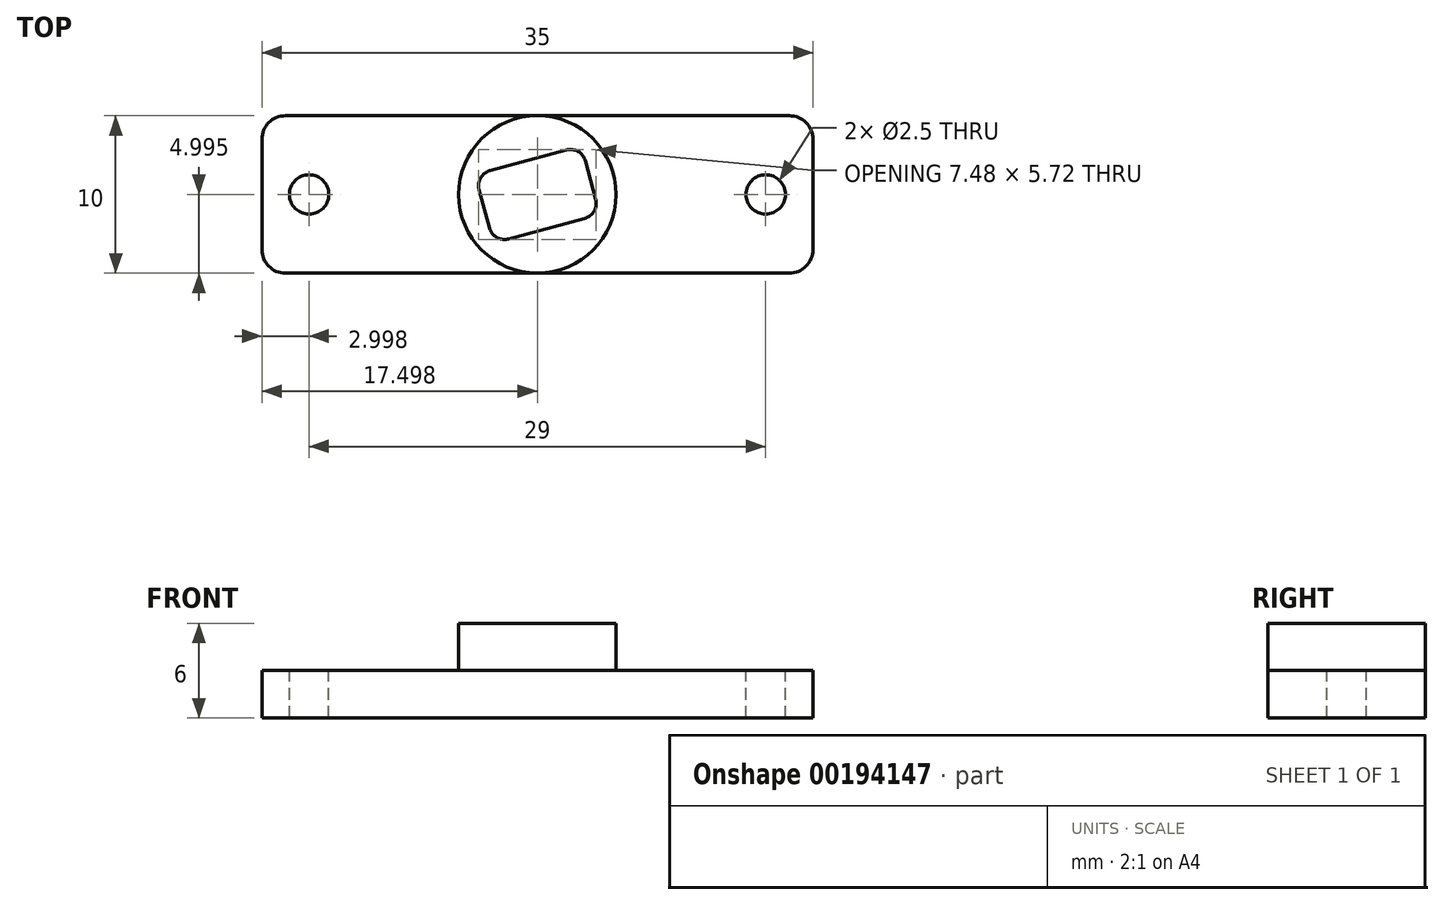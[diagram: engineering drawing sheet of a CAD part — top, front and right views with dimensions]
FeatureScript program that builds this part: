
annotation { "Feature Type Name" : "Feature", "Feature Type Description" : "" }
export const myFeature = defineFeature(function(context is Context, id is Id, definition is map)
    precondition{}
    {
        {
            var Q0;
            Q0=qCreatedBy(makeId("Top.planeOp"),FACE);
            var sketch = newSketch(context, id + "F0", { "sketchPlane" : qUnion([Q0])});
            skLineSegment(sketch, "E0.bottom", {"start": v(-6.32, 6.26) * mm, "end": v(28.68, 6.26) * mm});
            skLineSegment(sketch, "E0.top", {"start": v(-6.32, -3.74) * mm, "end": v(28.68, -3.74) * mm});
            skLineSegment(sketch, "E0.left", {"start": v(-6.32, 6.26) * mm, "end": v(-6.32, -3.74) * mm});
            skLineSegment(sketch, "E0.right", {"start": v(28.68, 6.26) * mm, "end": v(28.68, -3.74) * mm});
            skSolve(sketch);
        }
        {
            var Q0;
            Q0=makeQuery(id+"F0.imprint","IMPRINT",FACE,{"disambiguationData":[TD([[makeQuery(id+"F0.imprint","IMPRINT",EDGE,{"derivedFrom":sQuery(id+"F0.wireOp",EDGE,"E0.bottom")}),-1.0]])]});
            extrude(context, id + "F1", {"entities" : qUnion([Q0]), "depth" : 3 * mm});
        }
        {
            var Q0;
            Q0=makeQuery(id+"F1.opExtrude","SWEPT_EDGE",EDGE,{"disambiguationData":[OSD([sQuery(id+"F0.wireOp",EDGE,"E0.top"),sQuery(id+"F0.wireOp",EDGE,"E0.left")])]});
            var Q1;
            Q1=makeQuery(id+"F1.opExtrude","SWEPT_EDGE",EDGE,{"disambiguationData":[OSD([sQuery(id+"F0.wireOp",EDGE,"E0.bottom"),sQuery(id+"F0.wireOp",EDGE,"E0.left")])]});
            var Q2;
            Q2=makeQuery(id+"F1.opExtrude","SWEPT_EDGE",EDGE,{"disambiguationData":[OSD([sQuery(id+"F0.wireOp",EDGE,"E0.top"),sQuery(id+"F0.wireOp",EDGE,"E0.right")])]});
            var Q3;
            Q3=makeQuery(id+"F1.opExtrude","SWEPT_EDGE",EDGE,{"disambiguationData":[OSD([sQuery(id+"F0.wireOp",EDGE,"E0.bottom"),sQuery(id+"F0.wireOp",EDGE,"E0.right")])]});
            fillet(context, id + "F2", {"entities" : qUnion([Q0, Q1, Q2, Q3]), "radius" : 1.5 * mm, "tangentPropagation" : true, "allowEdgeOverflow" : false});
        }
        {
            var Q0;
            Q0=makeQuery(id+"F1.opExtrude","CAP_FACE",FACE,{"disambiguationData":[OSD([sQuery(id+"F0.wireOp",EDGE,"E0.bottom"),sQuery(id+"F0.wireOp",EDGE,"E0.top"),sQuery(id+"F0.wireOp",EDGE,"E0.left"),sQuery(id+"F0.wireOp",EDGE,"E0.right")])],"isStart":false});
            var sketch = newSketch(context, id + "F3", { "sketchPlane" : qUnion([Q0])});
            skCircle(sketch, "E1", {"center": v(11.18, 1.26) * mm, "radius": 5 * mm});
            skSolve(sketch);
        }
        {
            var Q0;
            {var subQ0=sQuery(id+"F3.wireOp",EDGE,"E1");var subQ1=makeQuery(id+"F3.imprint","INTERSECT",VERTEX,{"derivedFrom":[makeQuery(id+"F1.opExtrude","CAP_EDGE",EDGE,{"disambiguationData":[OSD([sQuery(id+"F0.wireOp",EDGE,"E0.bottom")])],"isStart":false}),subQ0]});Q0=makeQuery(id+"F3.imprint","IMPRINT",FACE,{"disambiguationData":[TD([[makeQuery(id+"F3.imprint","IMPRINT",EDGE,{"disambiguationData":[TD([[subQ1,-1.0]])],"derivedFrom":subQ0}),1.0]])]});}
            extrude(context, id + "F4", {"entities" : qUnion([Q0]), "operationType" : NewBodyOperationType.ADD, "depth" : 3 * mm});
        }
        {
            var Q0;
            Q0=makeQuery(id+"F4.opExtrude","CAP_FACE",FACE,{"disambiguationData":[OSD([sQuery(id+"F3.wireOp",EDGE,"E1")])],"isStart":false});
            var sketch = newSketch(context, id + "F5", { "sketchPlane" : qUnion([Q0])});
            skLineSegment(sketch, "E2.bottom", {"start": v(7.21, 2.51) * mm, "end": v(13.97, 4.34) * mm});
            skLineSegment(sketch, "E2.top", {"start": v(8.39, -1.83) * mm, "end": v(15.15, 0) * mm});
            skLineSegment(sketch, "E2.left", {"start": v(7.21, 2.51) * mm, "end": v(8.39, -1.83) * mm});
            skLineSegment(sketch, "E2.right", {"start": v(13.97, 4.34) * mm, "end": v(15.15, 0) * mm});
            skCircle(sketch, "E3", {"center": v(11.18, 1.26) * mm, "radius": 2.25 * mm});
            skSolve(sketch);
        }
        {
            var Q0;
            {var subQ0=sQuery(id+"F5.wireOp",EDGE,"E3");var subQ1=makeQuery(id+"F5.imprint","INTERSECT",VERTEX,{"derivedFrom":[sQuery(id+"F5.wireOp",EDGE,"E2.bottom"),subQ0]});Q0=makeQuery(id+"F5.imprint","IMPRINT",FACE,{"disambiguationData":[TD([[makeQuery(id+"F5.imprint","IMPRINT",EDGE,{"disambiguationData":[TD([[subQ1,-1.0]])],"derivedFrom":subQ0}),1.0]])]});}
            var Q1;
            {var subQ0=sQuery(id+"F5.wireOp",EDGE,"E2.right");Q1=makeQuery(id+"F5.imprint","IMPRINT",FACE,{"disambiguationData":[TD([[makeQuery(id+"F5.imprint","IMPRINT",EDGE,{"derivedFrom":subQ0}),-1.0]])]});}
            var Q2;
            {var subQ0=sQuery(id+"F5.wireOp",EDGE,"E2.left");Q2=makeQuery(id+"F5.imprint","IMPRINT",FACE,{"disambiguationData":[TD([[makeQuery(id+"F5.imprint","IMPRINT",EDGE,{"derivedFrom":subQ0}),1.0]])]});}
            extrude(context, id + "F6", {"entities" : qUnion([Q0, Q1, Q2]), "operationType" : NewBodyOperationType.REMOVE, "oppositeDirection" : true, "depth" : 6 * mm});
        }
        {
            var Q0;
            Q0=makeQuery(id+"F6.boolean.opBoolean","COPY",EDGE,{"derivedFrom":makeQuery(id+"F6.opExtrude","SWEPT_EDGE",EDGE,{"disambiguationData":[OSD([sQuery(id+"F5.wireOp",EDGE,"E2.bottom"),sQuery(id+"F5.wireOp",EDGE,"E2.left")])]})});
            var Q1;
            Q1=makeQuery(id+"F6.boolean.opBoolean","COPY",EDGE,{"derivedFrom":makeQuery(id+"F6.opExtrude","SWEPT_EDGE",EDGE,{"disambiguationData":[OSD([sQuery(id+"F5.wireOp",EDGE,"E2.top"),sQuery(id+"F5.wireOp",EDGE,"E2.left")])]})});
            var Q2;
            Q2=makeQuery(id+"F6.boolean.opBoolean","COPY",EDGE,{"derivedFrom":makeQuery(id+"F6.opExtrude","SWEPT_EDGE",EDGE,{"disambiguationData":[OSD([sQuery(id+"F5.wireOp",EDGE,"E2.top"),sQuery(id+"F5.wireOp",EDGE,"E2.right")])]})});
            var Q3;
            Q3=makeQuery(id+"F6.boolean.opBoolean","COPY",EDGE,{"derivedFrom":makeQuery(id+"F6.opExtrude","SWEPT_EDGE",EDGE,{"disambiguationData":[OSD([sQuery(id+"F5.wireOp",EDGE,"E2.bottom"),sQuery(id+"F5.wireOp",EDGE,"E2.right")])]})});
            fillet(context, id + "F7", {"entities" : qUnion([Q0, Q1, Q2, Q3]), "radius" : 1 * mm, "tangentPropagation" : true, "allowEdgeOverflow" : false});
        }
        {
            var Q0;
            {var subQ0=sQuery(id+"F0.wireOp",EDGE,"E0.left");var subQ1=sQuery(id+"F0.wireOp",EDGE,"E0.top");var subQ2=sQuery(id+"F0.wireOp",EDGE,"E0.bottom");var subQ3=makeQuery(id+"F1.opExtrude","CAP_FACE",FACE,{"disambiguationData":[OSD([subQ2,subQ1,subQ0,sQuery(id+"F0.wireOp",EDGE,"E0.right")])],"isStart":false});Q0=makeQuery(id+"F4.boolean.opBoolean","SPLIT",FACE,{"disambiguationData":[TD([makeQuery(id+"F1.opExtrude","SWEPT_FACE",FACE,{"disambiguationData":[OSD([subQ0])]})])],"derivedFrom":subQ3});}
            var sketch = newSketch(context, id + "F8", { "sketchPlane" : qUnion([Q0])});
            skCircle(sketch, "E4", {"center": v(-3.32, 1.26) * mm, "radius": 1.25 * mm});
            skSolve(sketch);
        }
        {
            var Q0;
            {var subQ0=sQuery(id+"F0.wireOp",EDGE,"E0.right");var subQ1=sQuery(id+"F0.wireOp",EDGE,"E0.top");var subQ2=sQuery(id+"F0.wireOp",EDGE,"E0.bottom");var subQ3=makeQuery(id+"F1.opExtrude","CAP_FACE",FACE,{"disambiguationData":[OSD([subQ2,subQ1,sQuery(id+"F0.wireOp",EDGE,"E0.left"),subQ0])],"isStart":false});Q0=makeQuery(id+"F4.boolean.opBoolean","SPLIT",FACE,{"disambiguationData":[TD([makeQuery(id+"F1.opExtrude","SWEPT_FACE",FACE,{"disambiguationData":[OSD([subQ0])]})])],"derivedFrom":subQ3});}
            var sketch = newSketch(context, id + "F9", { "sketchPlane" : qUnion([Q0])});
            skCircle(sketch, "E5", {"center": v(25.68, 1.26) * mm, "radius": 1.25 * mm});
            skSolve(sketch);
        }
        {
            var Q0;
            Q0=makeQuery(id+"F8.imprint","IMPRINT",FACE,{"disambiguationData":[TD([[makeQuery(id+"F8.imprint","IMPRINT",EDGE,{"derivedFrom":sQuery(id+"F8.wireOp",EDGE,"E4")}),1.0]])]});
            extrude(context, id + "F10", {"entities" : qUnion([Q0]), "operationType" : NewBodyOperationType.REMOVE, "oppositeDirection" : true, "depth" : 3 * mm});
        }
        {
            var Q0;
            Q0=makeQuery(id+"F9.imprint","IMPRINT",FACE,{"disambiguationData":[TD([[makeQuery(id+"F9.imprint","IMPRINT",EDGE,{"derivedFrom":sQuery(id+"F9.wireOp",EDGE,"E5")}),1.0]])]});
            extrude(context, id + "F11", {"entities" : qUnion([Q0]), "operationType" : NewBodyOperationType.REMOVE, "oppositeDirection" : true, "depth" : 3 * mm});
        }
    });
